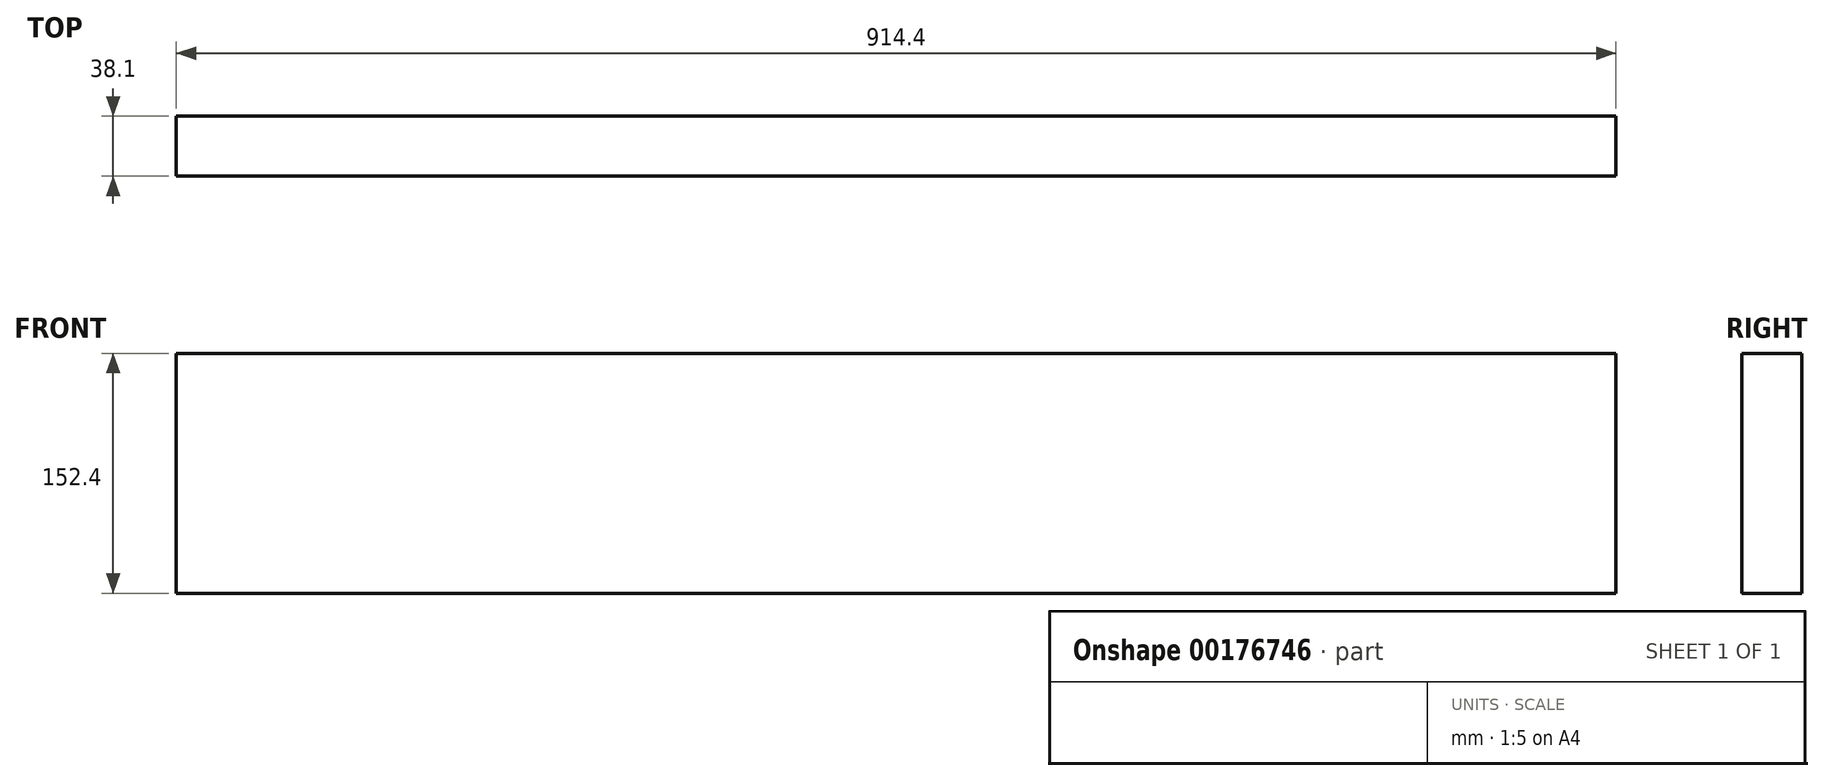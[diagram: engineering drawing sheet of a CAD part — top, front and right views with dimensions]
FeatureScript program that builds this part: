
annotation { "Feature Type Name" : "Feature", "Feature Type Description" : "" }
export const myFeature = defineFeature(function(context is Context, id is Id, definition is map)
    precondition{}
    {
        {
            var Q0;
            Q0=qCreatedBy(makeId("Front.planeOp"),FACE);
            var sketch = newSketch(context, id + "F0", { "sketchPlane" : qUnion([Q0])});
            skLineSegment(sketch, "E0.bottom", {"start": v(-298.83, 67.92) * mm, "end": v(615.57, 67.92) * mm});
            skLineSegment(sketch, "E0.top", {"start": v(-298.83, -84.48) * mm, "end": v(615.57, -84.48) * mm});
            skLineSegment(sketch, "E0.left", {"start": v(-298.83, -84.48) * mm, "end": v(-298.83, 67.92) * mm});
            skLineSegment(sketch, "E0.right", {"start": v(615.57, -84.48) * mm, "end": v(615.57, 67.92) * mm});
            skSolve(sketch);
        }
        {
            var Q0;
            Q0=makeQuery(id+"F0.imprint","IMPRINT",FACE,{"disambiguationData":[TD([[makeQuery(id+"F0.imprint","IMPRINT",EDGE,{"derivedFrom":sQuery(id+"F0.wireOp",EDGE,"E0.bottom")}),-1.0]])]});
            extrude(context, id + "F1", {"entities" : qUnion([Q0]), "depth" : 38.1 * mm});
        }
    });
